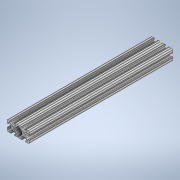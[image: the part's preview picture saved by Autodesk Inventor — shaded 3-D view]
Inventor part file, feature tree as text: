
AUTODESK INVENTOR PART (.ipt)
format: ipt  version: 2020 (Build 240168000, 168)  size: 333,824 bytes
history: native  units: in
note: dims shown in document units (in); Inventor stores cm internally (conversion verified against a paired STEP export)
features: sketch x2, extrude x1
ambient origin geometry x8: Origin, YZ Plane, XZ Plane, XY Plane, X Axis, Y Axis, Z Axis, Center Point
bodies: Solid1 (feature_tree)
feature tree (3):
  extrude  "Extrusion1"  [1 undecoded]
  sketch  "Sketch2"
  sketch  "Sketch1"  dims[d0=13.0in d1=0.0in]
note: 1 required parameter value undecoded (feature->parameter linkage not recoverable at this tier; creation-order binding heuristic only, values carry confidence <= 0.55)
